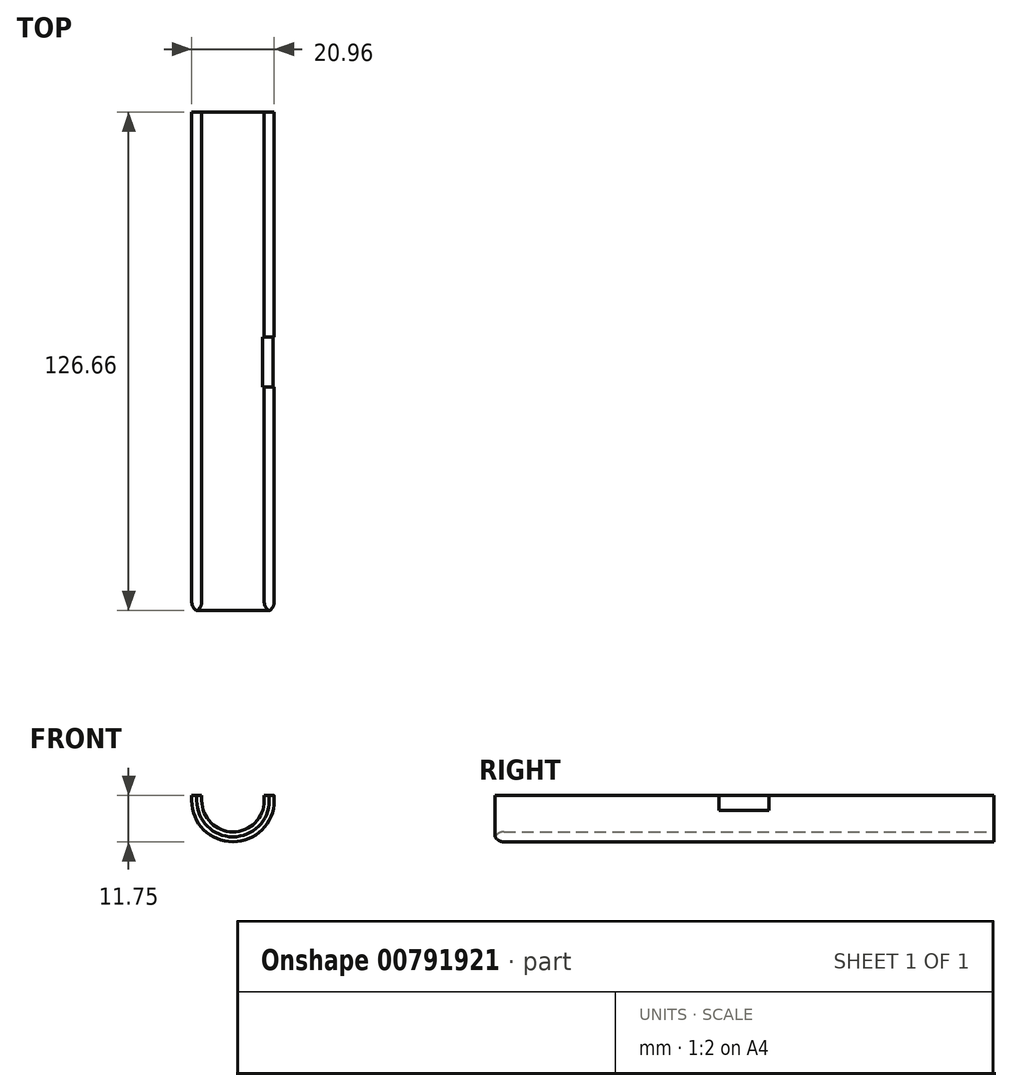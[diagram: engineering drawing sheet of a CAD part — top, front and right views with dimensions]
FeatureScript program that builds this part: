
annotation { "Feature Type Name" : "Feature", "Feature Type Description" : "" }
export const myFeature = defineFeature(function(context is Context, id is Id, definition is map)
    precondition{}
    {
        {
            var Q0;
            Q0=qCreatedBy(makeId("Front.planeOp"),FACE);
            var sketch = newSketch(context, id + "F0", { "sketchPlane" : qUnion([Q0])});
            skArc(sketch, "E0", {"start": v(-7.94, 0) * mm, "mid": v(0, -7.94) * mm, "end": v(7.94, 0) * mm});
            skLineSegment(sketch, "E1", {"start": v(7.94, 0) * mm, "end": v(10.48, 0) * mm, "construction": true});
            skLineSegment(sketch, "E2", {"start": v(0, 0) * mm, "end": v(0, -7.94) * mm});
            skLineSegment(sketch, "E3", {"start": v(-7.94, 0) * mm, "end": v(-10.48, 0) * mm, "construction": true});
            skLineSegment(sketch, "E4", {"start": v(0, -7.94) * mm, "end": v(0, -10.48) * mm, "construction": true});
            skArc(sketch, "E5", {"start": v(-10.48, 0) * mm, "mid": v(0, -10.48) * mm, "end": v(10.48, 0) * mm});
            skLineSegment(sketch, "E6.top", {"start": v(10.48, 1.27) * mm, "end": v(7.94, 1.27) * mm});
            skLineSegment(sketch, "E6.left", {"start": v(10.48, 0) * mm, "end": v(10.48, 1.27) * mm});
            skLineSegment(sketch, "E6.right", {"start": v(7.94, 0) * mm, "end": v(7.94, 1.27) * mm});
            skLineSegment(sketch, "E7.top", {"start": v(-10.48, 1.27) * mm, "end": v(-7.94, 1.27) * mm});
            skLineSegment(sketch, "E7.left", {"start": v(-10.48, 0) * mm, "end": v(-10.48, 1.27) * mm});
            skLineSegment(sketch, "E7.right", {"start": v(-7.94, 0) * mm, "end": v(-7.94, 1.27) * mm});
            skSolve(sketch);
        }
        {
            var Q0;
            Q0=makeQuery(id+"F0.imprint","IMPRINT",FACE,{"disambiguationData":[TD([[makeQuery(id+"F0.imprint","IMPRINT",EDGE,{"derivedFrom":sQuery(id+"F0.wireOp",EDGE,"E5")}),1.0]])]});
            extrude(context, id + "F1", {"entities" : qUnion([Q0]), "depth" : 127 * mm, "offsetDistance" : 25.4 * mm});
        }
        {
            var Q0;
            Q0=makeQuery(id+"F1.opExtrude","SWEPT_FACE",FACE,{"disambiguationData":[OSD([sQuery(id+"F0.wireOp",EDGE,"E6.left")])]});
            var sketch = newSketch(context, id + "F2", { "sketchPlane" : qUnion([Q0])});
            skLineSegment(sketch, "E8", {"start": v(-63.5, 0) * mm, "end": v(-69.85, 0) * mm, "construction": true});
            skLineSegment(sketch, "E9", {"start": v(-63.5, 0) * mm, "end": v(-57.15, 0) * mm, "construction": true});
            skLineSegment(sketch, "E10", {"start": v(-69.85, 0) * mm, "end": v(-69.85, 1.27) * mm});
            skLineSegment(sketch, "E11", {"start": v(-69.85, 1.27) * mm, "end": v(-57.15, 1.27) * mm});
            skLineSegment(sketch, "E12", {"start": v(-57.15, 1.27) * mm, "end": v(-57.15, 0) * mm});
            skLineSegment(sketch, "E13", {"start": v(-69.85, 0) * mm, "end": v(-69.85, -2.54) * mm});
            skLineSegment(sketch, "E14", {"start": v(-69.85, -2.54) * mm, "end": v(-57.15, -2.54) * mm});
            skLineSegment(sketch, "E15", {"start": v(-57.15, -2.54) * mm, "end": v(-57.15, 0) * mm});
            skSolve(sketch);
        }
        {
            var Q0;
            {var subQ0=sQuery(id+"F2.wireOp",EDGE,"E13");Q0=makeQuery(id+"F2.imprint","IMPRINT",FACE,{"disambiguationData":[TD([[makeQuery(id+"F2.imprint","IMPRINT",EDGE,{"derivedFrom":subQ0}),1.0]])]});}
            var Q1;
            {var subQ0=sQuery(id+"F2.wireOp",EDGE,"E10");Q1=makeQuery(id+"F2.imprint","IMPRINT",FACE,{"disambiguationData":[TD([[makeQuery(id+"F2.imprint","IMPRINT",EDGE,{"derivedFrom":subQ0}),-1.0]])]});}
            extrude(context, id + "F3", {"entities" : qUnion([Q0, Q1]), "operationType" : NewBodyOperationType.REMOVE, "oppositeDirection" : true, "depth" : 9.52 * mm, "offsetDistance" : 25.4 * mm});
        }
        {
            var Q0;
            Q0=makeQuery(id+"F1.opExtrude","CAP_EDGE",EDGE,{"disambiguationData":[OSD([sQuery(id+"F0.wireOp",EDGE,"E0")])],"isStart":false});
            var Q1;
            Q1=makeQuery(id+"F1.opExtrude","CAP_EDGE",EDGE,{"disambiguationData":[OSD([sQuery(id+"F0.wireOp",EDGE,"E5")])],"isStart":false});
            fillet(context, id + "F4", {"entities" : qUnion([Q0, Q1]), "radius" : 2.54 * mm, "tangentPropagation" : true, "allowEdgeOverflow" : false});
        }
    });
